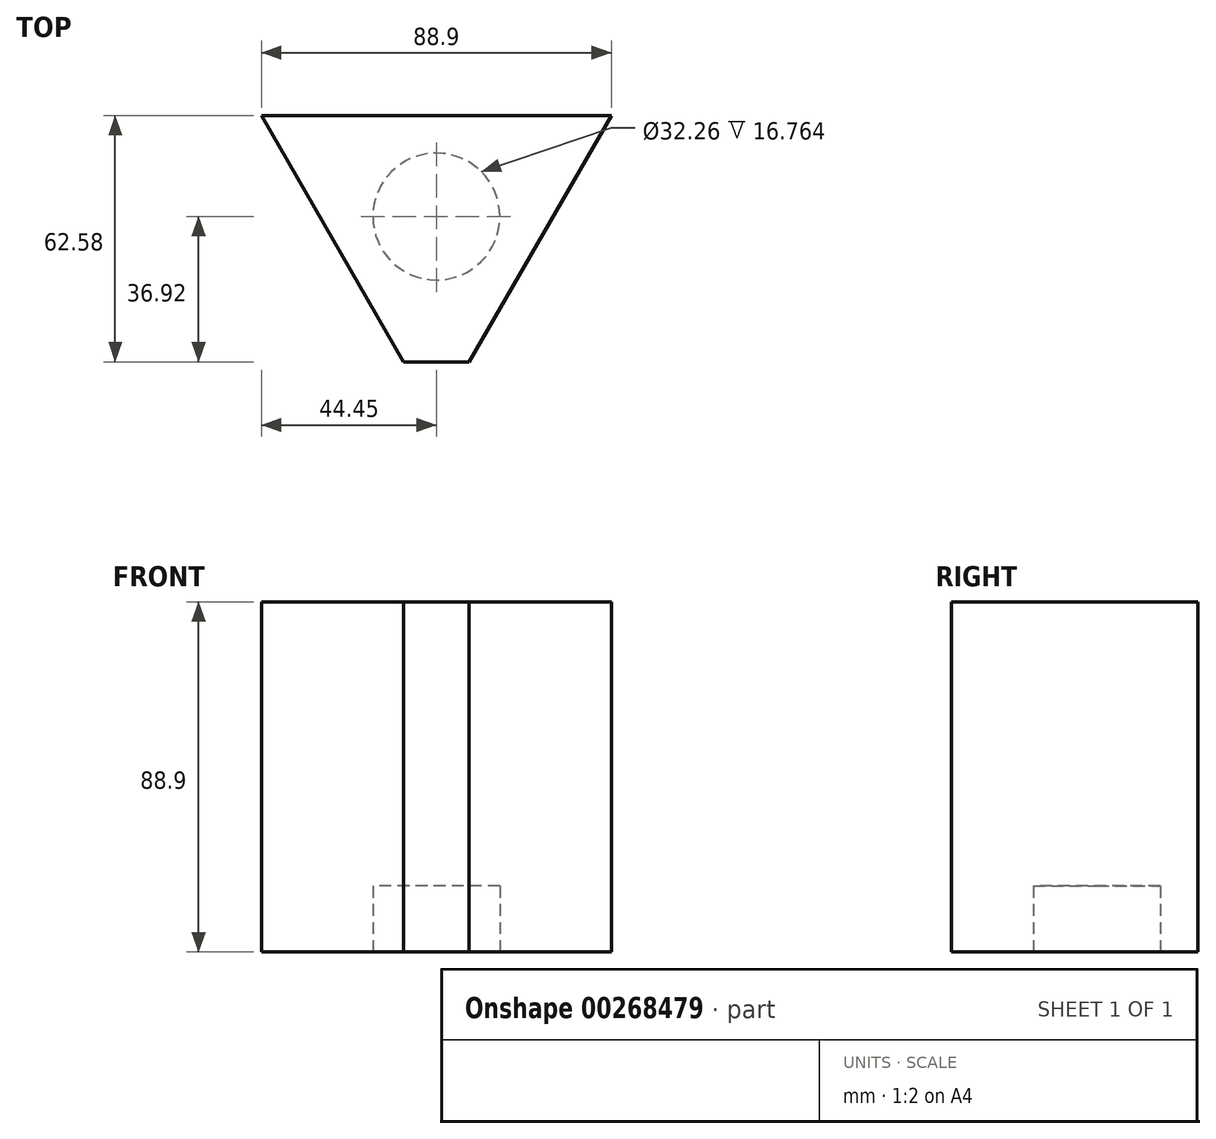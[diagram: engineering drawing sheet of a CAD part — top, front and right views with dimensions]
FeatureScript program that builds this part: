
annotation { "Feature Type Name" : "Feature", "Feature Type Description" : "" }
export const myFeature = defineFeature(function(context is Context, id is Id, definition is map)
    precondition{}
    {
        {
            var Q0;
            Q0=qCreatedBy(makeId("Top.planeOp"),FACE);
            var sketch = newSketch(context, id + "F0", { "sketchPlane" : qUnion([Q0])});
            skCircle(sketch, "E0.cCircle", {"center": v(0, 0) * mm, "radius": 25.66 * mm, "construction": true});
            skLineSegment(sketch, "E0.0", {"start": v(-44.45, 25.66) * mm, "end": v(44.45, 25.66) * mm});
            skLineSegment(sketch, "E0.1", {"start": v(44.45, 25.66) * mm, "end": v(0, -51.33) * mm});
            skLineSegment(sketch, "E0.2", {"start": v(0, -51.33) * mm, "end": v(-44.45, 25.66) * mm});
            skPoint(sketch, "E0.0.midPoint", {"position": v(0, 25.66) * mm});
            skSolve(sketch);
        }
        {
            var Q0;
            Q0=qSketchRegion(id+"F0",true);
            extrude(context, id + "F1", {"entities" : qUnion([Q0]), "depth" : 88.9 * mm});
        }
        {
            var Q0;
            Q0=qCreatedBy(makeId("Top.planeOp"),FACE);
            var sketch = newSketch(context, id + "F2", { "sketchPlane" : qUnion([Q0])});
            skLineSegment(sketch, "E1.bottom", {"start": v(-45.03, 26.58) * mm, "end": v(44.53, 26.58) * mm});
            skLineSegment(sketch, "E1.top", {"start": v(-45.03, -36.92) * mm, "end": v(44.53, -36.92) * mm});
            skLineSegment(sketch, "E1.left", {"start": v(-45.03, 26.58) * mm, "end": v(-45.03, -36.92) * mm});
            skLineSegment(sketch, "E1.right", {"start": v(44.53, 26.58) * mm, "end": v(44.53, -36.92) * mm});
            skSolve(sketch);
        }
        {
            var Q0;
            Q0=qSketchRegion(id+"F2",true);
            extrude(context, id + "F3", {"entities" : qUnion([Q0]), "operationType" : NewBodyOperationType.INTERSECT, "depth" : 215.9 * mm});
        }
        {
            var Q0;
            Q0=qCreatedBy(makeId("Top.planeOp"),FACE);
            var sketch = newSketch(context, id + "F4", { "sketchPlane" : qUnion([Q0])});
            skCircle(sketch, "E2", {"center": v(0, 0) * mm, "radius": 16.13 * mm});
            skSolve(sketch);
        }
        {
            var Q0;
            Q0=qSketchRegion(id+"F4",true);
            extrude(context, id + "F5", {"entities" : qUnion([Q0]), "operationType" : NewBodyOperationType.REMOVE, "depth" : 16.76 * mm});
        }
    });
